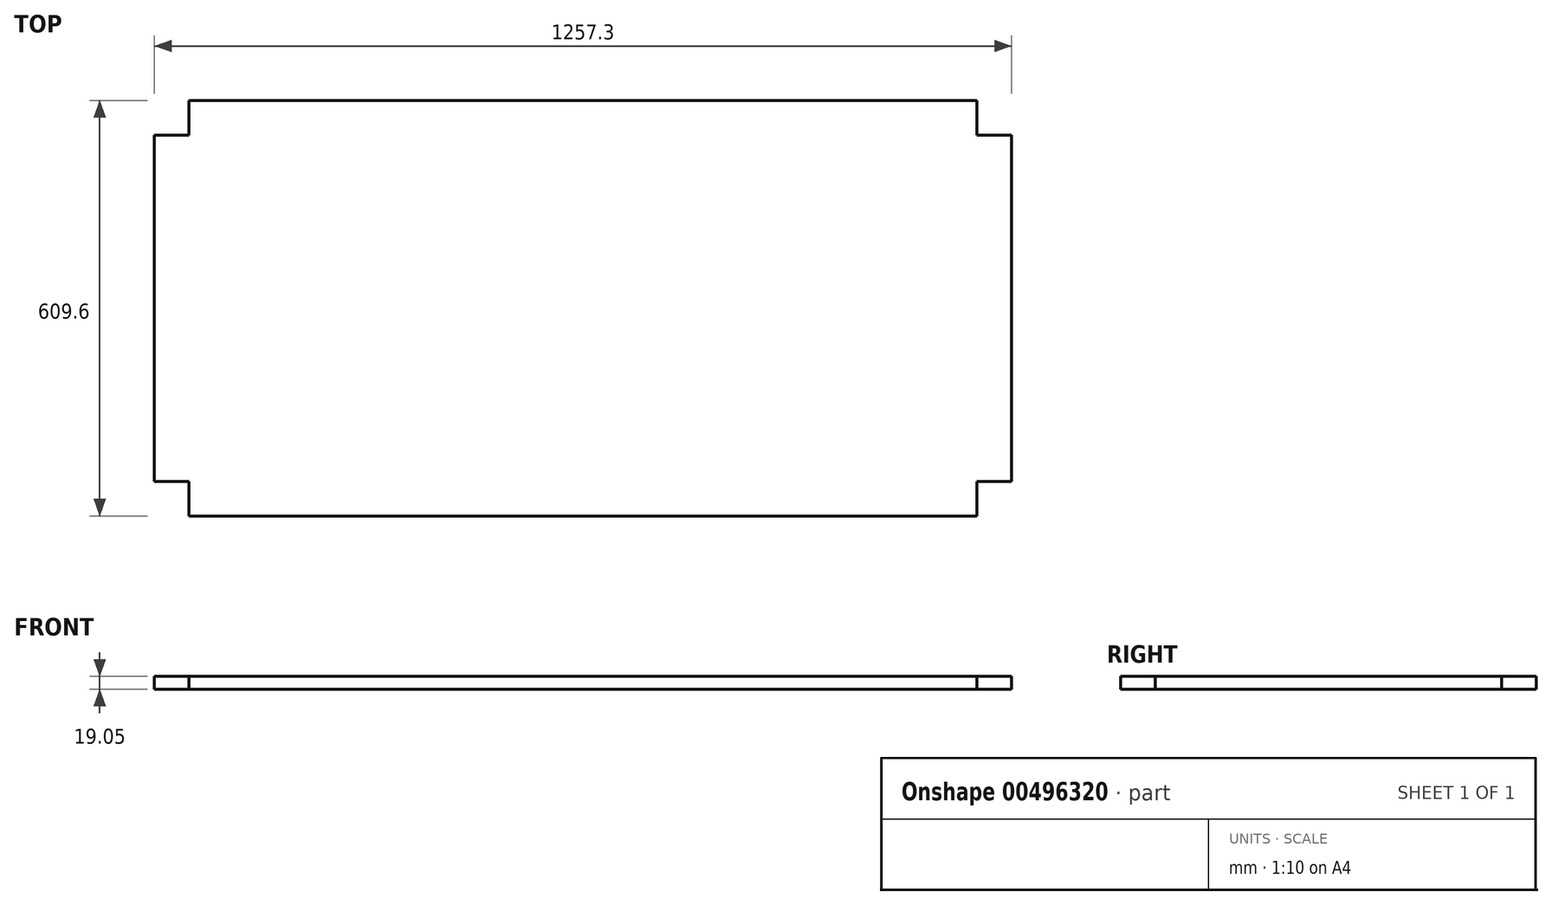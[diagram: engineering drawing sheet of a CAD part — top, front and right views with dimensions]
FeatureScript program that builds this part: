
annotation { "Feature Type Name" : "Feature", "Feature Type Description" : "" }
export const myFeature = defineFeature(function(context is Context, id is Id, definition is map)
    precondition{}
    {
        {
            var Q0;
            Q0=qCreatedBy(makeId("Top.planeOp"),FACE);
            var sketch = newSketch(context, id + "F0", { "sketchPlane" : qUnion([Q0])});
            skLineSegment(sketch, "E0.bottom", {"start": v(628.65, -304.8) * mm, "end": v(-628.65, -304.8) * mm});
            skLineSegment(sketch, "E0.top", {"start": v(628.65, 304.8) * mm, "end": v(-628.65, 304.8) * mm});
            skLineSegment(sketch, "E0.left", {"start": v(628.65, -304.8) * mm, "end": v(628.65, 304.8) * mm});
            skLineSegment(sketch, "E0.right", {"start": v(-628.65, -304.8) * mm, "end": v(-628.65, 304.8) * mm});
            skPoint(sketch, "E0.middle", {"position": v(0, 0) * mm});
            skSolve(sketch);
        }
        {
            var Q0;
            Q0=qSketchRegion(id+"F0",true);
            extrude(context, id + "F1", {"entities" : qUnion([Q0]), "depth" : 19.05 * mm});
        }
        {
            var Q0;
            Q0=makeQuery(id+"F1.opExtrude","CAP_FACE",FACE,{"disambiguationData":[OSD([sQuery(id+"F0.wireOp",EDGE,"E0.bottom"),sQuery(id+"F0.wireOp",EDGE,"E0.top"),sQuery(id+"F0.wireOp",EDGE,"E0.left"),sQuery(id+"F0.wireOp",EDGE,"E0.right")])],"isStart":false});
            var sketch = newSketch(context, id + "F2", { "sketchPlane" : qUnion([Q0])});
            skLineSegment(sketch, "E1.bottom", {"start": v(-628.65, 304.8) * mm, "end": v(-577.85, 304.8) * mm});
            skLineSegment(sketch, "E1.top", {"start": v(-628.65, 254) * mm, "end": v(-577.85, 254) * mm});
            skLineSegment(sketch, "E1.left", {"start": v(-628.65, 304.8) * mm, "end": v(-628.65, 254) * mm});
            skLineSegment(sketch, "E1.right", {"start": v(-577.85, 304.8) * mm, "end": v(-577.85, 254) * mm});
            skLineSegment(sketch, "E2.MirrorCS", {"start": v(628.65, 304.8) * mm, "end": v(577.85, 304.8) * mm});
            skLineSegment(sketch, "E3.MirrorCS", {"start": v(577.85, 304.8) * mm, "end": v(577.85, 254) * mm});
            skLineSegment(sketch, "E4.MirrorCS", {"start": v(628.65, 254) * mm, "end": v(577.85, 254) * mm});
            skLineSegment(sketch, "E5.MirrorCS", {"start": v(628.65, 304.8) * mm, "end": v(628.65, 254) * mm});
            skLineSegment(sketch, "E6.MirrorCS", {"start": v(-628.65, -304.8) * mm, "end": v(-577.85, -304.8) * mm});
            skLineSegment(sketch, "E7.MirrorCS", {"start": v(-577.85, -304.8) * mm, "end": v(-577.85, -254) * mm});
            skLineSegment(sketch, "E8.MirrorCS", {"start": v(-628.65, -254) * mm, "end": v(-577.85, -254) * mm});
            skLineSegment(sketch, "E9.MirrorCS", {"start": v(-628.65, -304.8) * mm, "end": v(-628.65, -254) * mm});
            skLineSegment(sketch, "E10.MirrorCS", {"start": v(577.85, -304.8) * mm, "end": v(577.85, -254) * mm});
            skLineSegment(sketch, "E11.MirrorCS", {"start": v(628.65, -254) * mm, "end": v(577.85, -254) * mm});
            skLineSegment(sketch, "E12.MirrorCS", {"start": v(628.65, -304.8) * mm, "end": v(628.65, -254) * mm});
            skLineSegment(sketch, "E13.MirrorCS", {"start": v(628.65, -304.8) * mm, "end": v(577.85, -304.8) * mm});
            skSolve(sketch);
        }
        {
            var Q0;
            Q0 = qSketchRegion(id + "F2", true);
            extrude(context, id + "F3", {"entities" : qUnion([Q0]), "operationType" : NewBodyOperationType.REMOVE, "oppositeDirection" : true, "depth" : 38.1 * mm});
        }
    });
